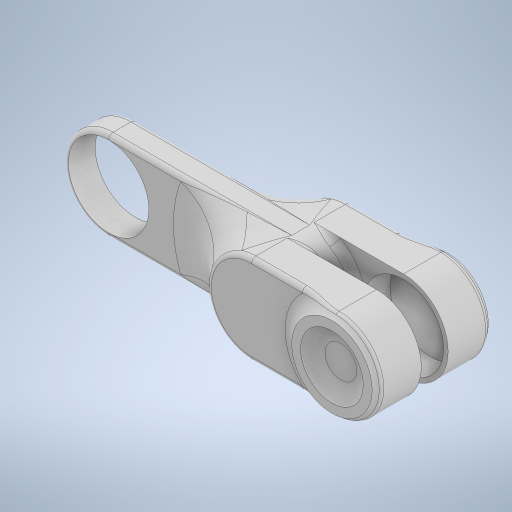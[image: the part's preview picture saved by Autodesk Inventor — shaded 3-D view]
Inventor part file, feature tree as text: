
AUTODESK INVENTOR PART (.ipt)
format: ipt  version: 2024 (Build 280153000, 153)  size: 528,384 bytes
history: native  units: mm
features: sketch x6, extrude x5, fillet x4, mirror x1
ambient origin geometry x8: Origin, YZ Plane, XZ Plane, XY Plane, X Axis, Y Axis, Z Axis, Center Point
bodies: Solid1 (feature_tree)
feature tree (16):
  extrude  "Extrusion1"  Depth=100.0mm
  extrude  "Extrusion2"  Depth=200.0mm
  extrude  "Extrusion3"  Depth=100.0mm TaperAngle=0.0deg
  fillet  "Fillet2"  Radius=100.0mm
  extrude  "Extrusion4"  Depth=90.0mm
  fillet  "Fillet3"  Radius=40.0mm
  mirror  "Mirror1"
  fillet  "Fillet6"  Radius=90.0mm
  fillet  "Fillet7"  Radius=70.0mm
  sketch  "Sketch9"  dims[d41=10.0mm d42=0.0mm d43=20.0mm]
  extrude  "Extrusion5"  Depth=20.0mm
  sketch  "Sketch5"  dims[d25=90.0mm d26=100.0mm]
  sketch  "Sketch6"  dims[d27=200.0mm d28=200.0mm]
  sketch  "Sketch7"  dims[d29=50.0mm d30=15.0mm d31=0.0mm d32=100.0mm]
  sketch  "Sketch8"  dims[d34=100.0mm d35=50.0mm d36=40.0mm d37=0.0mm d39=90.0mm d40=70.0mm]
  sketch  "Sketch10"  dims[d44=90.0mm d45=30.0mm d46=0.0mm d47=5.0mm d50=8.0mm d51=100.0mm d53=14.0mm d54=12.0mm d55=20.0mm d56=2.5mm d57=2.5mm d58=100.0mm d59=0.0mm]
